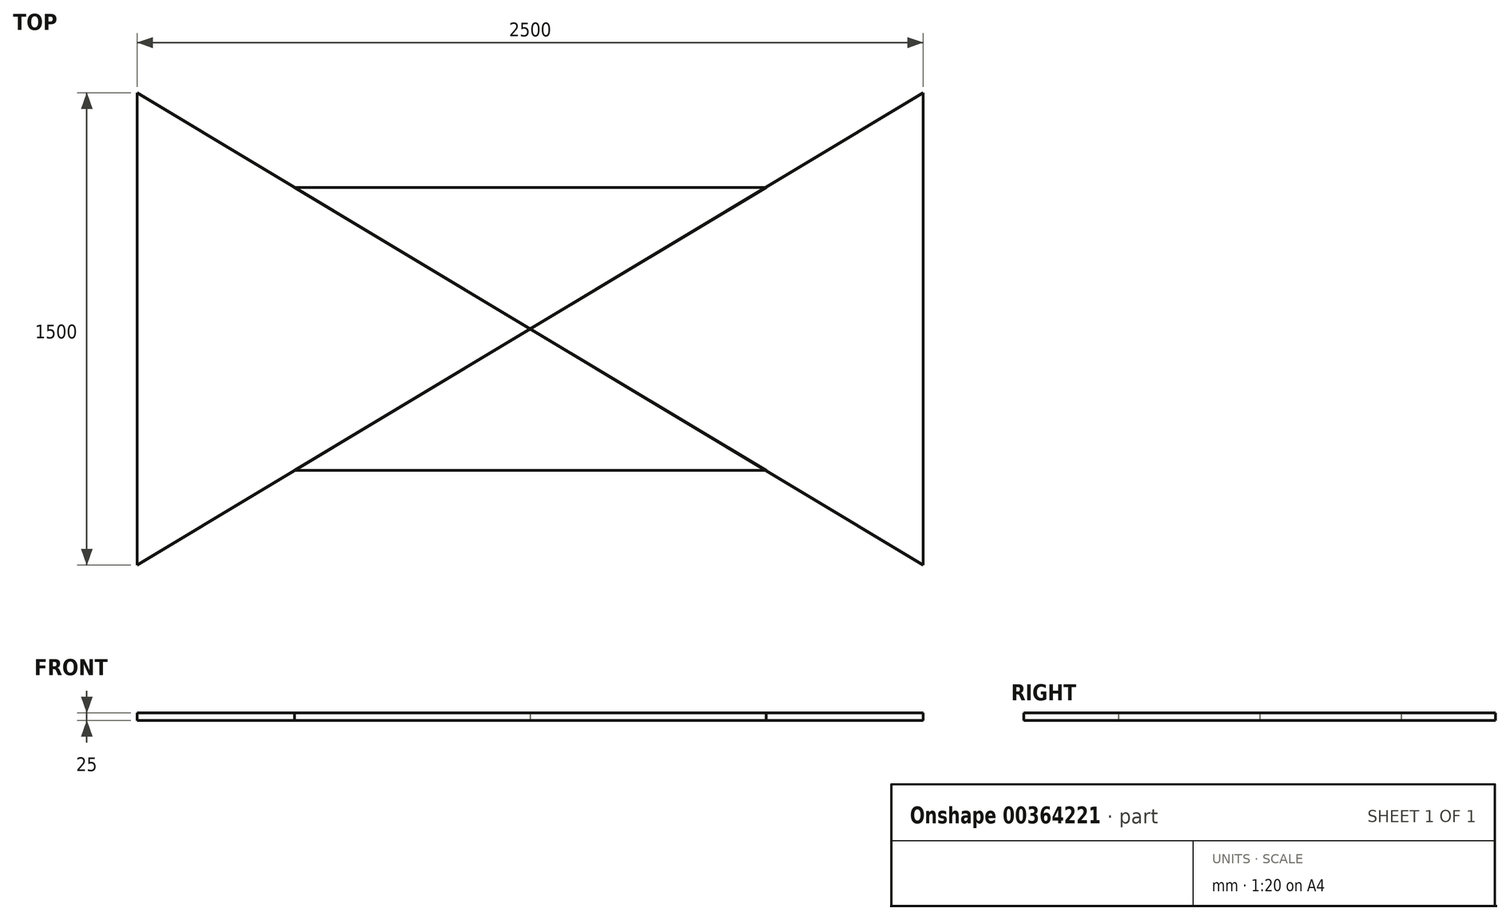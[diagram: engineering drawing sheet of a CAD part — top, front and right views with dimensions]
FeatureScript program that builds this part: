
annotation { "Feature Type Name" : "Feature", "Feature Type Description" : "" }
export const myFeature = defineFeature(function(context is Context, id is Id, definition is map)
    precondition{}
    {
        {
            var Q0;
            Q0=qCreatedBy(makeId("Top.planeOp"),FACE);
            var sketch = newSketch(context, id + "F0", { "sketchPlane" : qUnion([Q0])});
            skLineSegment(sketch, "E0", {"start": v(-2954.5, 1806.23) * mm, "end": v(-2954.5, -2533.77) * mm});
            skLineSegment(sketch, "E1", {"start": v(-2954.5, -2533.77) * mm, "end": v(3097, -1280.07) * mm});
            skLineSegment(sketch, "E2", {"start": v(3097, -1280.07) * mm, "end": v(2811.99, 2007.6) * mm});
            skLineSegment(sketch, "E3", {"start": v(2811.99, 2007.6) * mm, "end": v(-2954.5, 1806.23) * mm});
            skLineSegment(sketch, "E4", {"start": v(71.25, -1906.92) * mm, "end": v(-71.25, 1906.92) * mm, "construction": true});
            skSolve(sketch);
        }
        {
            var Q0;
            Q0=qCreatedBy(makeId("Top.planeOp"),FACE);
            var sketch = newSketch(context, id + "F1", { "sketchPlane" : qUnion([Q0])});
            skLineSegment(sketch, "E5.bottom", {"start": v(1250, -750) * mm, "end": v(-1250, -750) * mm});
            skLineSegment(sketch, "E5.top", {"start": v(1250, 750) * mm, "end": v(-1250, 750) * mm});
            skLineSegment(sketch, "E5.left", {"start": v(1250, -750) * mm, "end": v(1250, 750) * mm});
            skLineSegment(sketch, "E5.right", {"start": v(-1250, -750) * mm, "end": v(-1250, 750) * mm});
            skPoint(sketch, "E5.middle", {"position": v(0, 0) * mm});
            skLineSegment(sketch, "E6", {"start": v(-1250, -750) * mm, "end": v(1250, 750) * mm});
            skLineSegment(sketch, "E7", {"start": v(-1250, 750) * mm, "end": v(1250, -750) * mm});
            skLineSegment(sketch, "E8", {"start": v(-1250, 450) * mm, "end": v(1250, 450) * mm});
            skLineSegment(sketch, "E9", {"start": v(1250, 450) * mm, "end": v(1250, 450) * mm});
            skLineSegment(sketch, "E10", {"start": v(1250, -450) * mm, "end": v(-1250, -450) * mm});
            skLineSegment(sketch, "E11", {"start": v(0, 450) * mm, "end": v(0, -450) * mm, "construction": true});
            skLineSegment(sketch, "E12", {"start": v(-960.21, 1875.87) * mm, "end": v(-960.21, 1275.87) * mm});
            skLineSegment(sketch, "E13.0", {"start": v(2811.99, 2007.6) * mm, "end": v(-2954.5, 1806.23) * mm});
            skLineSegment(sketch, "E14.0", {"start": v(-2954.5, 1806.23) * mm, "end": v(-2954.5, -2533.77) * mm});
            skLineSegment(sketch, "E15.0", {"start": v(-2954.5, -2533.77) * mm, "end": v(3097, -1280.07) * mm});
            skSolve(sketch);
        }
        {
            var Q0;
            {var subQ1=sQuery(id+"F1.wireOp",EDGE,"E5.left");var subQ3=sQuery(id+"F1.wireOp",EDGE,"E10");var subQ4=makeQuery(id+"F1.imprint","INTERSECT",VERTEX,{"derivedFrom":[subQ1,subQ3]});Q0=makeQuery(id+"F1.imprint","IMPRINT",FACE,{"disambiguationData":[TD([[makeQuery(id+"F1.imprint","IMPRINT",EDGE,{"disambiguationData":[TD([[subQ4,-1.0]])],"derivedFrom":subQ3}),1.0]])]});}
            var Q1;
            {var subQ1=sQuery(id+"F1.wireOp",EDGE,"E5.left");var subQ3=sQuery(id+"F1.wireOp",EDGE,"E8");var subQ4=makeQuery(id+"F1.imprint","INTERSECT",VERTEX,{"derivedFrom":[subQ1,subQ3]});Q1=makeQuery(id+"F1.imprint","IMPRINT",FACE,{"disambiguationData":[TD([[makeQuery(id+"F1.imprint","IMPRINT",EDGE,{"disambiguationData":[TD([[subQ4,1.0]])],"derivedFrom":subQ3}),1.0]])]});}
            var Q2;
            {var subQ1=sQuery(id+"F1.wireOp",EDGE,"E5.right");var subQ3=sQuery(id+"F1.wireOp",EDGE,"E10");var subQ4=makeQuery(id+"F1.imprint","INTERSECT",VERTEX,{"derivedFrom":[subQ1,subQ3]});Q2=makeQuery(id+"F1.imprint","IMPRINT",FACE,{"disambiguationData":[TD([[makeQuery(id+"F1.imprint","IMPRINT",EDGE,{"disambiguationData":[TD([[subQ4,1.0]])],"derivedFrom":subQ3}),1.0]])]});}
            var Q3;
            {var subQ1=sQuery(id+"F1.wireOp",EDGE,"E5.right");var subQ3=sQuery(id+"F1.wireOp",EDGE,"E8");var subQ4=makeQuery(id+"F1.imprint","INTERSECT",VERTEX,{"derivedFrom":[subQ1,subQ3]});Q3=makeQuery(id+"F1.imprint","IMPRINT",FACE,{"disambiguationData":[TD([[makeQuery(id+"F1.imprint","IMPRINT",EDGE,{"disambiguationData":[TD([[subQ4,-1.0]])],"derivedFrom":subQ3}),1.0]])]});}
            var Q4;
            {var subQ5=sQuery(id+"F1.wireOp",EDGE,"E8");var subQ6=sQuery(id+"F1.wireOp",EDGE,"E5.left");var subQ7=makeQuery(id+"F1.imprint","INTERSECT",VERTEX,{"derivedFrom":[subQ6,subQ5]});Q4=makeQuery(id+"F1.imprint","IMPRINT",FACE,{"disambiguationData":[TD([[makeQuery(id+"F1.imprint","IMPRINT",EDGE,{"disambiguationData":[TD([[subQ7,1.0]])],"derivedFrom":subQ6}),1.0]])]});}
            var Q5;
            {var subQ3=sQuery(id+"F1.wireOp",EDGE,"E8");var subQ7=sQuery(id+"F1.wireOp",EDGE,"E5.right");var subQ8=makeQuery(id+"F1.imprint","INTERSECT",VERTEX,{"derivedFrom":[subQ7,subQ3]});Q5=makeQuery(id+"F1.imprint","IMPRINT",FACE,{"disambiguationData":[TD([[makeQuery(id+"F1.imprint","IMPRINT",EDGE,{"disambiguationData":[TD([[subQ8,1.0]])],"derivedFrom":subQ7}),-1.0]])]});}
            extrude(context, id + "F2", {"entities" : qUnion([Q0, Q1, Q2, Q3, Q4, Q5]), "depth" : 25 * mm});
        }
        {
            var Q0;
            {var subQ0=sQuery(id+"F1.wireOp",EDGE,"E7");var subQ1=sQuery(id+"F1.wireOp",EDGE,"E6");var subQ2=makeQuery(id+"F1.imprint","INTERSECT",VERTEX,{"derivedFrom":[subQ1,subQ0]});Q0=makeQuery(id+"F1.imprint","IMPRINT",FACE,{"disambiguationData":[TD([[makeQuery(id+"F1.imprint","IMPRINT",EDGE,{"disambiguationData":[TD([[subQ2,-1.0]])],"derivedFrom":subQ1}),1.0]])]});}
            var Q1;
            {var subQ0=sQuery(id+"F1.wireOp",EDGE,"E10");var subQ1=sQuery(id+"F1.wireOp",EDGE,"E6");var subQ2=makeQuery(id+"F1.imprint","INTERSECT",VERTEX,{"derivedFrom":[subQ1,subQ0]});Q1=makeQuery(id+"F1.imprint","IMPRINT",FACE,{"disambiguationData":[TD([[makeQuery(id+"F1.imprint","IMPRINT",EDGE,{"disambiguationData":[TD([[subQ2,-1.0]])],"derivedFrom":subQ1}),-1.0]])]});}
            extrude(context, id + "F3", {"entities" : qUnion([Q0, Q1]), "depth" : 25 * mm});
        }
    });
